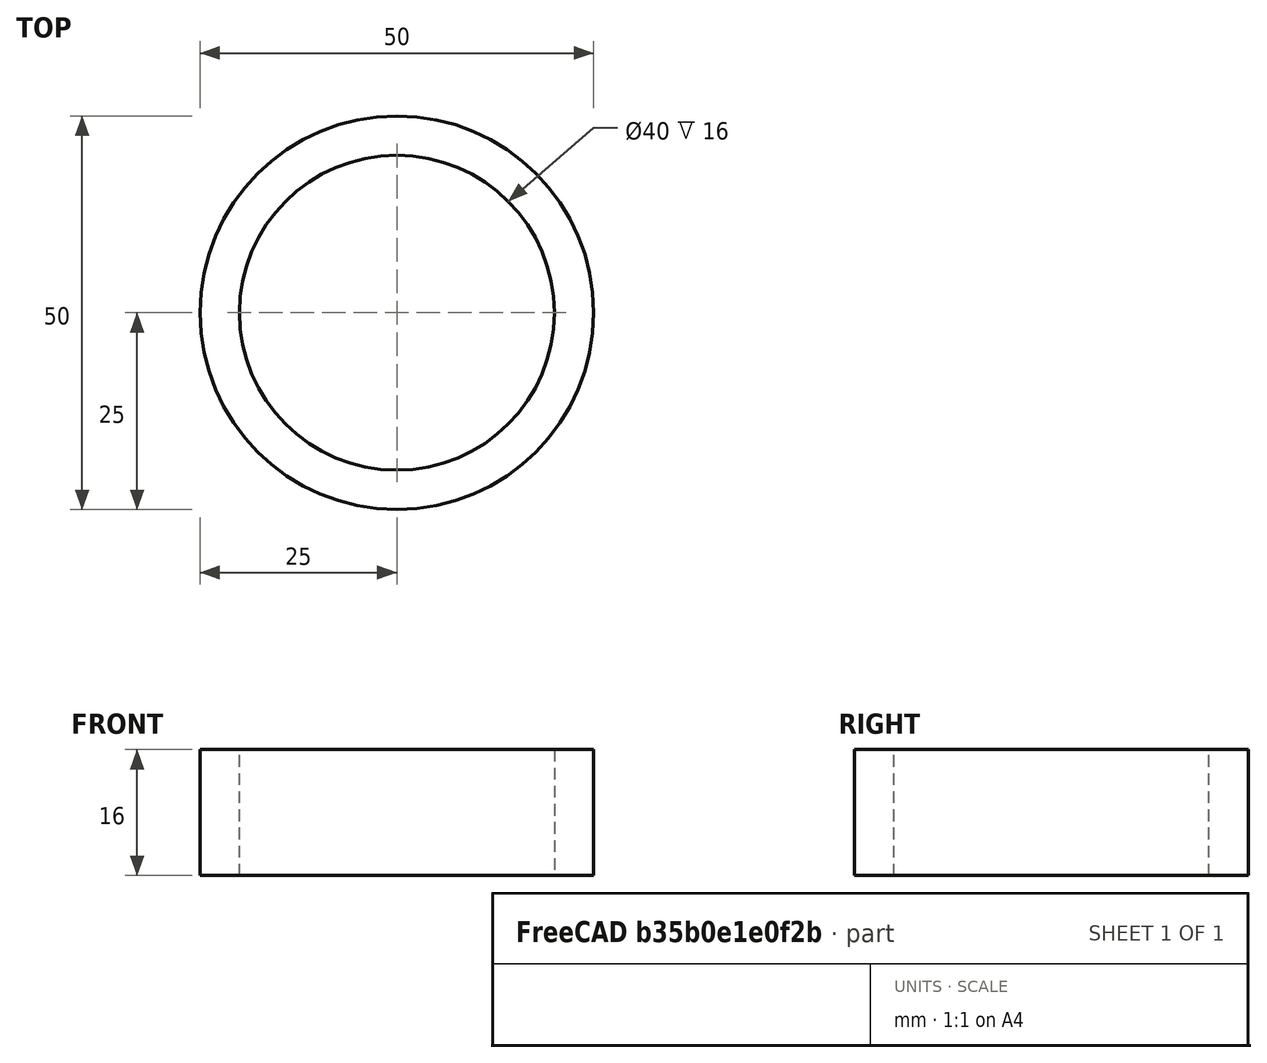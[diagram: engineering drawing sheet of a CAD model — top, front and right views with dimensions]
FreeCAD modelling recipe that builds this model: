
FCSTD DOCUMENT  (FreeCAD 1.0R39319 (Git))
Label: cilindro_tubular_50x40x16
License: All rights reserved
LicenseURL: https://en.wikipedia.org/wiki/All_rights_reserved
objects: Sketcher::SketchObject×2, PartDesign::Pad×1, PartDesign::Pocket×1, PartDesign::Body×1
note: 11 computed .brp shape members not serialized (recipe doc carries the construction recipe); baked Part::Feature solids carry a one-line shape summary decoded from their .brp

FEATURE [Sketcher::SketchObject] Sketch_1
  ArcFitTolerance = 1e-06
  AttachmentSupport = -> [XY_Plane]
  FullyConstrained = false
  MakeInternals = false
  MapMode = 5
  sketch-geometry (1):
    g0: Circle CenterX=0 CenterY=0 CenterZ=0 NormalX=0 NormalY=0 NormalZ=1 AngleXU=0 Radius=25
FEATURE [PartDesign::Pad] Pad_1
  Direction = (0,0,1)
  Length = 16
  Length2 = 10
  Profile = -> Sketch_1
  Refine = true
  Suppressed = false
  Type = 0
FEATURE [Sketcher::SketchObject] Sketch_2
  ArcFitTolerance = 1e-06
  AttachmentSupport = -> [Pad_1]
  FullyConstrained = false
  MakeInternals = false
  MapMode = 5
  Placement = pos=(0,0,16) rot=(0,0,1;0rad)
  sketch-geometry (1):
    g0: Circle CenterX=0 CenterY=0 CenterZ=0 NormalX=0 NormalY=0 NormalZ=1 AngleXU=0 Radius=20
FEATURE [PartDesign::Pocket] Pocket_2
  BaseFeature = -> Pad_1
  Direction = (0,0,-1)
  Length = 5
  Length2 = 5
  Profile = -> Sketch_2
  Refine = true
  Suppressed = false
  Type = 1
FEATURE [PartDesign::Body] Body
  AllowCompound = false
  Group = -> [Sketch_1,Pad_1,Sketch_2,Pocket_2]
  Origin = -> Origin
  Tip = -> Pocket_2
